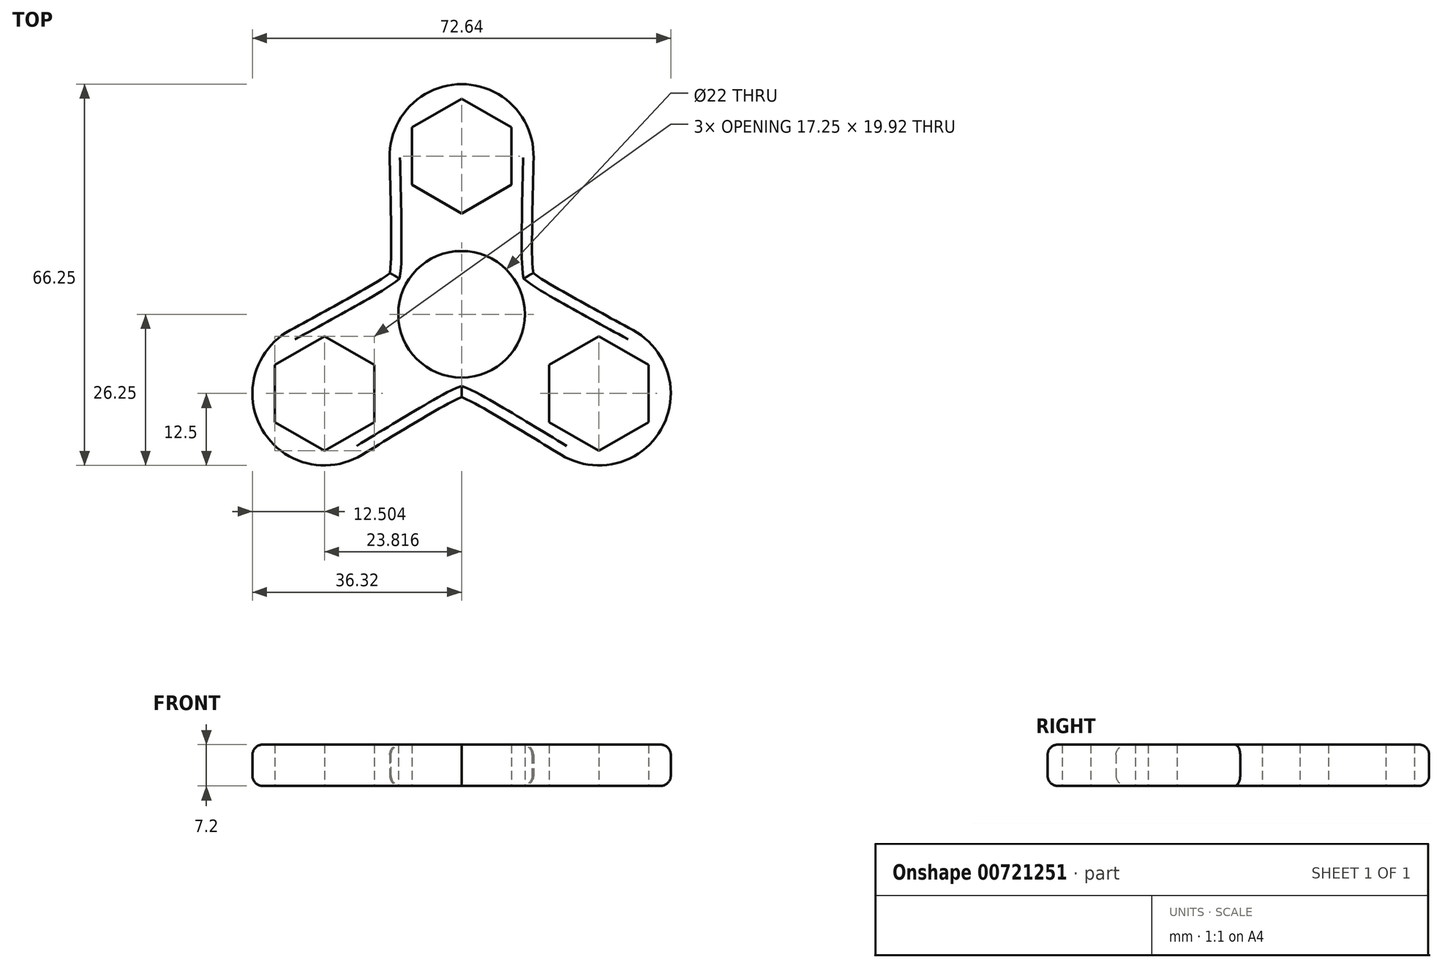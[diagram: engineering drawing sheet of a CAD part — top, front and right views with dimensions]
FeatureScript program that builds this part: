
annotation { "Feature Type Name" : "Feature", "Feature Type Description" : "" }
export const myFeature = defineFeature(function(context is Context, id is Id, definition is map)
    precondition{}
    {
        {
            var Q0;
            Q0=qCreatedBy(makeId("Top.planeOp"),FACE);
            var sketch = newSketch(context, id + "F0", { "sketchPlane" : qUnion([Q0])});
            skCircle(sketch, "E0", {"center": v(0, 0) * mm, "radius": 11 * mm});
            skCircle(sketch, "E1.cCircle", {"center": v(0, 27.5) * mm, "radius": 8.63 * mm, "construction": true});
            skLineSegment(sketch, "E1.0", {"start": v(-8.62, 22.52) * mm, "end": v(-8.62, 32.48) * mm});
            skLineSegment(sketch, "E1.1", {"start": v(-8.62, 32.48) * mm, "end": v(0, 37.46) * mm});
            skLineSegment(sketch, "E1.2", {"start": v(0, 37.46) * mm, "end": v(8.63, 32.48) * mm});
            skLineSegment(sketch, "E1.3", {"start": v(8.63, 32.48) * mm, "end": v(8.63, 22.52) * mm});
            skLineSegment(sketch, "E1.4", {"start": v(8.63, 22.52) * mm, "end": v(0, 17.54) * mm});
            skLineSegment(sketch, "E1.5", {"start": v(0, 17.54) * mm, "end": v(-8.62, 22.52) * mm});
            skPoint(sketch, "E1.0.midPoint", {"position": v(-8.62, 27.5) * mm});
            skArc(sketch, "E2", {"start": v(12.5, 27.16) * mm, "mid": v(0, 40) * mm, "end": v(-12.5, 27.16) * mm});
            skFitSpline(sketch, "E3", {"points": [v(-14, 0) * mm, v(-12.25, 10) * mm, v(-12.5, 27.16) * mm], "startDerivative": vector(11.4, 47.73) * mm, "endDerivative": vector(-1.33, 49.34) * mm});
            skLineSegment(sketch, "E4", {"start": v(-32.38, 10) * mm, "end": v(49.75, 10) * mm, "construction": true});
            skFitSpline(sketch, "E5.MirrorCS", {"points": [v(14, 0) * mm, v(12.25, 10) * mm, v(12.5, 27.16) * mm], "startDerivative": vector(-11.4, 47.73) * mm, "endDerivative": vector(1.33, 49.34) * mm});
            skLineSegment(sketch, "E6", {"start": v(-50.14, -28.95) * mm, "end": v(62.45, 36.05) * mm, "construction": true});
            skLineSegment(sketch, "E7", {"start": v(-59.52, 34.36) * mm, "end": v(53.06, -30.64) * mm, "construction": true});
            skFitSpline(sketch, "E8.MirrorCS", {"points": [v(-7, -12.12) * mm, v(2.54, -15.6) * mm, v(17.28, -24.4) * mm], "startDerivative": vector(47.04, -13.99) * mm, "endDerivative": vector(42.07, -25.82) * mm});
            skFitSpline(sketch, "E9.MirrorCS", {"points": [v(7, 12.12) * mm, v(14.78, 5.6) * mm, v(29.77, -2.76) * mm], "startDerivative": vector(35.63, -33.74) * mm, "endDerivative": vector(43.4, -23.52) * mm});
            skArc(sketch, "E10.MirrorC", {"start": v(29.77, -2.76) * mm, "mid": v(34.64, -20) * mm, "end": v(17.28, -24.4) * mm});
            skCircle(sketch, "E11.MirrorC", {"center": v(23.82, -13.75) * mm, "radius": 8.63 * mm, "construction": true});
            skLineSegment(sketch, "E12.MirrorCS", {"start": v(32.44, -8.77) * mm, "end": v(23.82, -3.8) * mm});
            skLineSegment(sketch, "E13.MirrorCS", {"start": v(23.82, -3.8) * mm, "end": v(15.2, -8.77) * mm});
            skPoint(sketch, "E14.MirrorP", {"position": v(19.5, -21.22) * mm});
            skLineSegment(sketch, "E15.MirrorCS", {"start": v(32.44, -18.73) * mm, "end": v(32.44, -8.77) * mm});
            skLineSegment(sketch, "E16.MirrorCS", {"start": v(23.82, -23.7) * mm, "end": v(32.44, -18.73) * mm});
            skLineSegment(sketch, "E17.MirrorCS", {"start": v(15.2, -8.77) * mm, "end": v(15.2, -18.73) * mm});
            skLineSegment(sketch, "E18.MirrorCS", {"start": v(15.2, -18.73) * mm, "end": v(23.82, -23.7) * mm});
            skLineSegment(sketch, "E19.MirrorCS", {"start": v(-23.82, -3.8) * mm, "end": v(-32.44, -8.77) * mm});
            skLineSegment(sketch, "E20.MirrorCS", {"start": v(-23.82, -23.7) * mm, "end": v(-15.2, -18.73) * mm});
            skFitSpline(sketch, "E21.MirrorCS", {"points": [v(7, -12.12) * mm, v(-2.54, -15.6) * mm, v(-17.28, -24.4) * mm], "startDerivative": vector(-47.04, -13.99) * mm, "endDerivative": vector(-42.07, -25.82) * mm});
            skFitSpline(sketch, "E22.MirrorCS", {"points": [v(-7, 12.12) * mm, v(-14.78, 5.6) * mm, v(-29.77, -2.76) * mm], "startDerivative": vector(-35.63, -33.74) * mm, "endDerivative": vector(-43.4, -23.52) * mm});
            skArc(sketch, "E23.MirrorC", {"start": v(-17.28, -24.4) * mm, "mid": v(-34.64, -20) * mm, "end": v(-29.77, -2.76) * mm});
            skLineSegment(sketch, "E24.MirrorCS", {"start": v(-15.2, -8.77) * mm, "end": v(-23.82, -3.8) * mm});
            skLineSegment(sketch, "E25.MirrorCS", {"start": v(-15.2, -18.73) * mm, "end": v(-15.2, -8.77) * mm});
            skPoint(sketch, "E26.MirrorP", {"position": v(-28.13, -6.28) * mm});
            skLineSegment(sketch, "E27.MirrorCS", {"start": v(-32.44, -18.73) * mm, "end": v(-23.82, -23.7) * mm});
            skLineSegment(sketch, "E28.MirrorCS", {"start": v(-32.44, -8.77) * mm, "end": v(-32.44, -18.73) * mm});
            skCircle(sketch, "E29.MirrorC", {"center": v(-23.82, -13.75) * mm, "radius": 8.63 * mm, "construction": true});
            skSolve(sketch);
        }
        {
            var Q0;
            Q0=makeQuery(id+"F0.imprint","IMPRINT",FACE,{"disambiguationData":[TD([[makeQuery(id+"F0.imprint","IMPRINT",EDGE,{"derivedFrom":sQuery(id+"F0.wireOp",EDGE,"E0")}),-1.0]])]});
            extrude(context, id + "F1", {"entities" : qUnion([Q0]), "depth" : 7.2 * mm, "offsetDistance" : 25 * mm});
        }
        {
            var Q0;
            Q0=makeQuery(id+"F1.opExtrude","CAP_EDGE",EDGE,{"disambiguationData":[OSD([sQuery(id+"F0.wireOp",EDGE,"E2")])],"isStart":false});
            var Q1;
            Q1=makeQuery(id+"F1.opExtrude","CAP_EDGE",EDGE,{"disambiguationData":[OSD([sQuery(id+"F0.wireOp",EDGE,"E10.MirrorC")])],"isStart":false});
            var Q2;
            Q2=makeQuery(id+"F1.opExtrude","CAP_EDGE",EDGE,{"disambiguationData":[OSD([sQuery(id+"F0.wireOp",EDGE,"E23.MirrorC")])],"isStart":false});
            var Q3;
            Q3=makeQuery(id+"F1.opExtrude","CAP_EDGE",EDGE,{"disambiguationData":[OSD([sQuery(id+"F0.wireOp",EDGE,"E2")])],"isStart":true});
            var Q4;
            Q4=makeQuery(id+"F1.opExtrude","CAP_EDGE",EDGE,{"disambiguationData":[OSD([sQuery(id+"F0.wireOp",EDGE,"E10.MirrorC")])],"isStart":true});
            var Q5;
            Q5=makeQuery(id+"F1.opExtrude","CAP_EDGE",EDGE,{"disambiguationData":[OSD([sQuery(id+"F0.wireOp",EDGE,"E23.MirrorC")])],"isStart":true});
            fillet(context, id + "F2", {"entities" : qUnion([Q0, Q1, Q2, Q3, Q4, Q5]), "radius" : 1.8 * mm, "tangentPropagation" : true, "allowEdgeOverflow" : false});
        }
    });
